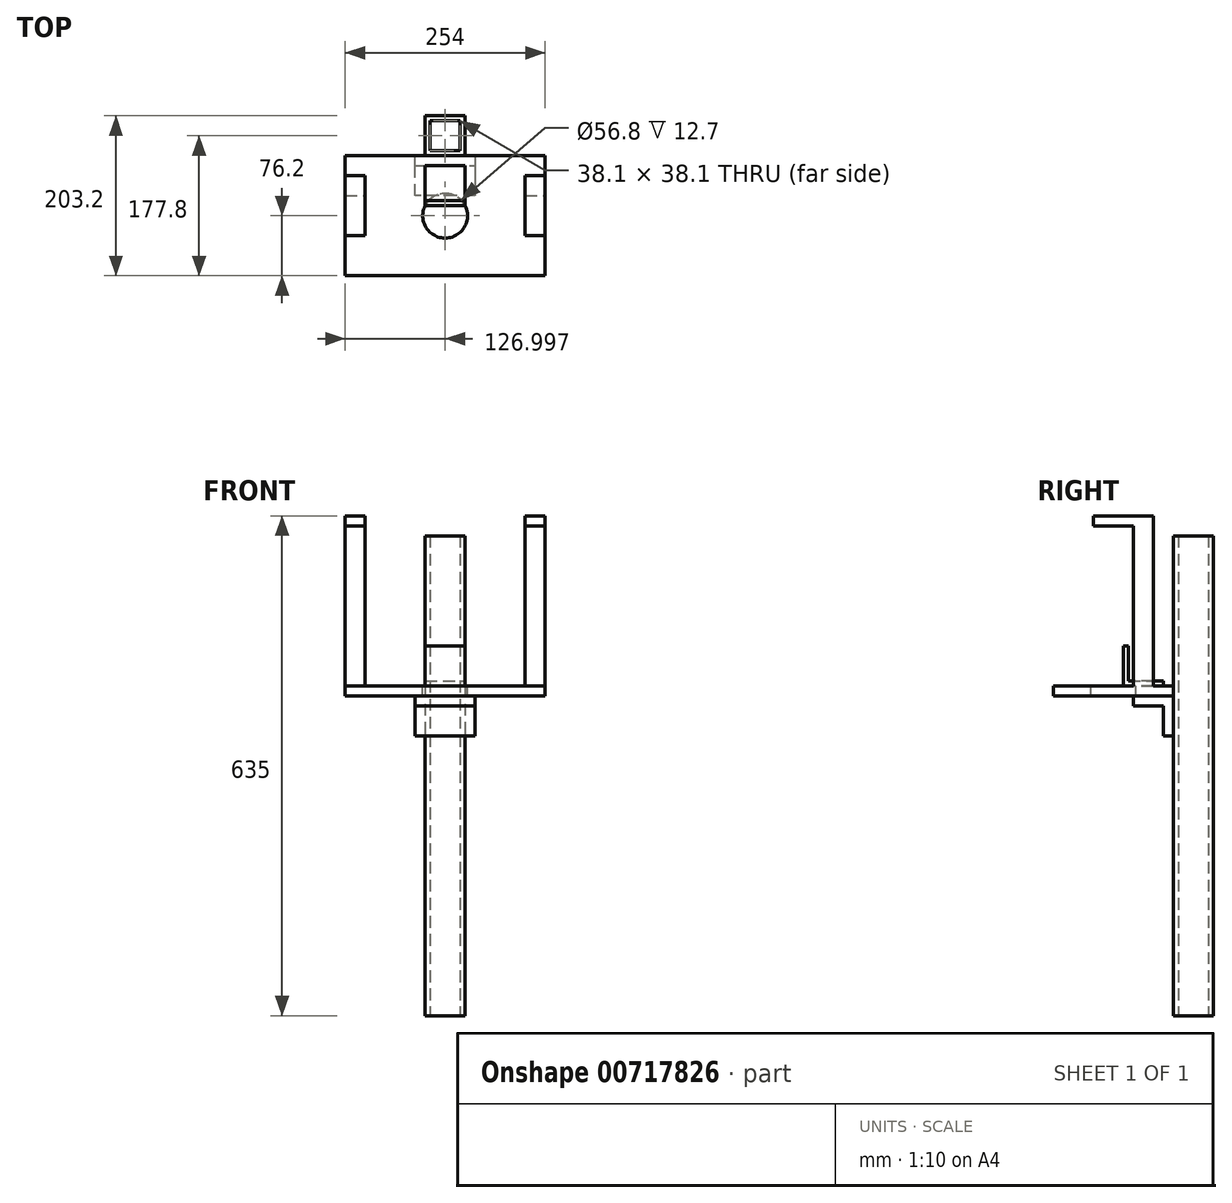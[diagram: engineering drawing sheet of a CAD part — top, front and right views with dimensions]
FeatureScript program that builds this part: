
annotation { "Feature Type Name" : "Feature", "Feature Type Description" : "" }
export const myFeature = defineFeature(function(context is Context, id is Id, definition is map)
    precondition{}
    {
        {
            var Q0;
            Q0=qCreatedBy(makeId("Top.planeOp"),FACE);
            var sketch = newSketch(context, id + "F0", { "sketchPlane" : qUnion([Q0])});
            skLineSegment(sketch, "E0.bottom", {"start": v(3.34, 0) * mm, "end": v(257.34, 0) * mm});
            skLineSegment(sketch, "E0.top", {"start": v(3.34, 152.4) * mm, "end": v(257.34, 152.4) * mm});
            skLineSegment(sketch, "E0.left", {"start": v(3.34, 0) * mm, "end": v(3.34, 152.4) * mm});
            skLineSegment(sketch, "E0.right", {"start": v(257.34, 0) * mm, "end": v(257.34, 152.4) * mm});
            skSolve(sketch);
        }
        {
            var Q0;
            Q0 = qSketchRegion(id + "F0", true);
            extrude(context, id + "F1", {"entities" : qUnion([Q0]), "depth" : 12.7 * mm, "offsetDistance" : 25.4 * mm});
        }
        {
            var Q0;
            Q0=makeQuery(id+"F1.opExtrude","CAP_FACE",FACE,{"disambiguationData":[OSD([sQuery(id+"F0.wireOp",EDGE,"E0.bottom"),sQuery(id+"F0.wireOp",EDGE,"E0.top"),sQuery(id+"F0.wireOp",EDGE,"E0.left"),sQuery(id+"F0.wireOp",EDGE,"E0.right")])],"isStart":false});
            var sketch = newSketch(context, id + "F2", { "sketchPlane" : qUnion([Q0])});
            skLineSegment(sketch, "E1", {"start": v(3.34, 88.9) * mm, "end": v(104.94, 88.9) * mm});
            skLineSegment(sketch, "E2", {"start": v(104.94, 88.9) * mm, "end": v(104.94, 139.7) * mm});
            skLineSegment(sketch, "E3", {"start": v(104.94, 139.7) * mm, "end": v(155.74, 139.7) * mm});
            skLineSegment(sketch, "E4", {"start": v(155.74, 139.7) * mm, "end": v(155.74, 88.9) * mm});
            skLineSegment(sketch, "E5", {"start": v(155.74, 88.9) * mm, "end": v(104.94, 88.9) * mm});
            skSolve(sketch);
        }
        {
            var Q0;
            Q0 = qSketchRegion(id + "F2", true);
            extrude(context, id + "F3", {"entities" : qUnion([Q0]), "operationType" : NewBodyOperationType.ADD, "depth" : 6.35 * mm, "offsetDistance" : 25.4 * mm});
        }
        {
            var Q0;
            Q0=makeQuery(id+"F3.opExtrude","CAP_FACE",FACE,{"disambiguationData":[OSD([sQuery(id+"F2.wireOp",EDGE,"E2"),sQuery(id+"F2.wireOp",EDGE,"E3"),sQuery(id+"F2.wireOp",EDGE,"E4"),sQuery(id+"F2.wireOp",EDGE,"E5")])],"isStart":false});
            var sketch = newSketch(context, id + "F4", { "sketchPlane" : qUnion([Q0])});
            skLineSegment(sketch, "E6", {"start": v(104.94, 88.9) * mm, "end": v(104.94, 95.25) * mm});
            skLineSegment(sketch, "E7", {"start": v(104.94, 95.25) * mm, "end": v(155.74, 95.25) * mm});
            skLineSegment(sketch, "E8", {"start": v(155.74, 95.25) * mm, "end": v(155.74, 88.9) * mm});
            skLineSegment(sketch, "E9", {"start": v(155.74, 88.9) * mm, "end": v(104.94, 88.9) * mm});
            skSolve(sketch);
        }
        {
            var Q0;
            Q0 = qSketchRegion(id + "F4", true);
            extrude(context, id + "F5", {"entities" : qUnion([Q0]), "operationType" : NewBodyOperationType.ADD, "depth" : 44.45 * mm, "offsetDistance" : 25.4 * mm});
        }
        {
            var Q0;
            Q0=makeQuery(id+"F1.opExtrude","CAP_FACE",FACE,{"disambiguationData":[OSD([sQuery(id+"F0.wireOp",EDGE,"E0.bottom"),sQuery(id+"F0.wireOp",EDGE,"E0.top"),sQuery(id+"F0.wireOp",EDGE,"E0.left"),sQuery(id+"F0.wireOp",EDGE,"E0.right")])],"isStart":false});
            var sketch = newSketch(context, id + "F6", { "sketchPlane" : qUnion([Q0])});
            skLineSegment(sketch, "E10", {"start": v(155.74, 88.9) * mm, "end": v(104.94, 88.9) * mm});
            skCircle(sketch, "E11", {"center": v(130.34, 76.2) * mm, "radius": 28.4 * mm});
            skSolve(sketch);
        }
        {
            var Q0;
            Q0 = qSketchRegion(id + "F6", true);
            extrude(context, id + "F7", {"entities" : qUnion([Q0]), "operationType" : NewBodyOperationType.REMOVE, "oppositeDirection" : true, "depth" : 25.4 * mm, "offsetDistance" : 25.4 * mm});
        }
        {
            var Q0;
            Q0=makeQuery(id+"F1.opExtrude","CAP_FACE",FACE,{"disambiguationData":[OSD([sQuery(id+"F0.wireOp",EDGE,"E0.bottom"),sQuery(id+"F0.wireOp",EDGE,"E0.top"),sQuery(id+"F0.wireOp",EDGE,"E0.left"),sQuery(id+"F0.wireOp",EDGE,"E0.right")])],"isStart":true});
            var sketch = newSketch(context, id + "F8", { "sketchPlane" : qUnion([Q0])});
            skLineSegment(sketch, "E12", {"start": v(130.34, -152.4) * mm, "end": v(168.44, -152.4) * mm});
            skLineSegment(sketch, "E13", {"start": v(168.44, -152.4) * mm, "end": v(168.44, -101.6) * mm});
            skLineSegment(sketch, "E14", {"start": v(168.44, -101.6) * mm, "end": v(92.24, -101.6) * mm});
            skLineSegment(sketch, "E15", {"start": v(92.24, -101.6) * mm, "end": v(92.24, -152.4) * mm});
            skLineSegment(sketch, "E16", {"start": v(92.24, -152.4) * mm, "end": v(130.34, -152.4) * mm});
            skSolve(sketch);
        }
        {
            var Q0;
            Q0 = qSketchRegion(id + "F8", true);
            extrude(context, id + "F9", {"entities" : qUnion([Q0]), "operationType" : NewBodyOperationType.ADD, "depth" : 12.7 * mm, "offsetDistance" : 25.4 * mm});
        }
        {
            var Q0;
            Q0=makeQuery(id+"F9.opExtrude","CAP_FACE",FACE,{"disambiguationData":[OSD([sQuery(id+"F8.wireOp",EDGE,"E12"),sQuery(id+"F8.wireOp",EDGE,"E13"),sQuery(id+"F8.wireOp",EDGE,"E14"),sQuery(id+"F8.wireOp",EDGE,"E15"),sQuery(id+"F8.wireOp",EDGE,"E16")])],"isStart":false});
            var sketch = newSketch(context, id + "F10", { "sketchPlane" : qUnion([Q0])});
            skLineSegment(sketch, "E17", {"start": v(92.24, -152.4) * mm, "end": v(92.24, -139.7) * mm});
            skLineSegment(sketch, "E18", {"start": v(92.24, -139.7) * mm, "end": v(168.44, -139.7) * mm});
            skLineSegment(sketch, "E19", {"start": v(168.44, -139.7) * mm, "end": v(168.44, -152.4) * mm});
            skLineSegment(sketch, "E20", {"start": v(168.44, -152.4) * mm, "end": v(92.24, -152.4) * mm});
            skSolve(sketch);
        }
        {
            var Q0;
            Q0 = qSketchRegion(id + "F10", true);
            extrude(context, id + "F11", {"entities" : qUnion([Q0]), "operationType" : NewBodyOperationType.ADD, "depth" : 38.1 * mm, "offsetDistance" : 25.4 * mm});
        }
        {
            var Q0;
            Q0=makeQuery(id+"F11.boolean.opBoolean","MERGE",FACE,{"derivedFrom":[makeQuery(id+"F9.boolean.opBoolean","MERGE",FACE,{"derivedFrom":[makeQuery(id+"F1.opExtrude","SWEPT_FACE",FACE,{"disambiguationData":[OSD([sQuery(id+"F0.wireOp",EDGE,"E0.top")])]}),makeQuery(id+"F9.opExtrude","SWEPT_FACE",FACE,{"disambiguationData":[OSD([sQuery(id+"F8.wireOp",EDGE,"E12"),sQuery(id+"F8.wireOp",EDGE,"E16")])]})]}),makeQuery(id+"F11.opExtrude","SWEPT_FACE",FACE,{"disambiguationData":[OSD([sQuery(id+"F10.wireOp",EDGE,"E20")])]})]});
            var sketch = newSketch(context, id + "F12", { "sketchPlane" : qUnion([Q0])});
            skLineSegment(sketch, "E21", {"start": v(-130.34, 203.2) * mm, "end": v(-155.74, 203.2) * mm});
            skLineSegment(sketch, "E22", {"start": v(-155.74, 203.2) * mm, "end": v(-155.74, -406.4) * mm});
            skLineSegment(sketch, "E23", {"start": v(-130.34, 203.2) * mm, "end": v(-104.94, 203.2) * mm});
            skLineSegment(sketch, "E24", {"start": v(-104.94, 203.2) * mm, "end": v(-104.94, -406.4) * mm});
            skLineSegment(sketch, "E25", {"start": v(-104.94, -406.4) * mm, "end": v(-155.74, -406.4) * mm});
            skSolve(sketch);
        }
        {
            var Q0;
            Q0 = qSketchRegion(id + "F12", true);
            extrude(context, id + "F13", {"entities" : qUnion([Q0]), "operationType" : NewBodyOperationType.ADD, "depth" : 50.8 * mm, "offsetDistance" : 25.4 * mm});
        }
        {
            var Q0;
            Q0=makeQuery(id+"F13.opExtrude","SWEPT_FACE",FACE,{"disambiguationData":[OSD([sQuery(id+"F12.wireOp",EDGE,"E25")])]});
            var sketch = newSketch(context, id + "F14", { "sketchPlane" : qUnion([Q0])});
            skLineSegment(sketch, "E26", {"start": v(104.94, -196.85) * mm, "end": v(111.29, -196.85) * mm});
            skLineSegment(sketch, "E27", {"start": v(111.29, -196.85) * mm, "end": v(111.29, -158.75) * mm});
            skLineSegment(sketch, "E28", {"start": v(111.29, -158.75) * mm, "end": v(149.39, -158.75) * mm});
            skLineSegment(sketch, "E29", {"start": v(149.39, -158.75) * mm, "end": v(149.39, -196.85) * mm});
            skLineSegment(sketch, "E30", {"start": v(149.39, -196.85) * mm, "end": v(111.29, -196.85) * mm});
            skSolve(sketch);
        }
        {
            var Q0;
            Q0 = qSketchRegion(id + "F14", true);
            extrude(context, id + "F15", {"entities" : qUnion([Q0]), "operationType" : NewBodyOperationType.REMOVE, "oppositeDirection" : true, "depth" : 647.7 * mm, "offsetDistance" : 25.4 * mm});
        }
        {
            var Q0;
            Q0=makeQuery(id+"F1.opExtrude","CAP_FACE",FACE,{"disambiguationData":[OSD([sQuery(id+"F0.wireOp",EDGE,"E0.bottom"),sQuery(id+"F0.wireOp",EDGE,"E0.top"),sQuery(id+"F0.wireOp",EDGE,"E0.left"),sQuery(id+"F0.wireOp",EDGE,"E0.right")])],"isStart":false});
            var sketch = newSketch(context, id + "F16", { "sketchPlane" : qUnion([Q0])});
            skLineSegment(sketch, "E31", {"start": v(3.34, 127) * mm, "end": v(28.74, 127) * mm});
            skLineSegment(sketch, "E32", {"start": v(28.74, 127) * mm, "end": v(28.74, 101.6) * mm});
            skLineSegment(sketch, "E33", {"start": v(3.34, 127) * mm, "end": v(3.34, 101.6) * mm});
            skLineSegment(sketch, "E34", {"start": v(3.34, 101.6) * mm, "end": v(28.74, 101.6) * mm});
            skLineSegment(sketch, "E35", {"start": v(257.34, 127) * mm, "end": v(231.94, 127) * mm});
            skLineSegment(sketch, "E36", {"start": v(231.94, 127) * mm, "end": v(231.94, 101.6) * mm});
            skLineSegment(sketch, "E37", {"start": v(231.94, 101.6) * mm, "end": v(257.34, 101.6) * mm});
            skLineSegment(sketch, "E38", {"start": v(257.34, 101.6) * mm, "end": v(257.34, 127) * mm});
            skSolve(sketch);
        }
        {
            var Q0;
            Q0 = qSketchRegion(id + "F16", true);
            extrude(context, id + "F17", {"entities" : qUnion([Q0]), "operationType" : NewBodyOperationType.ADD, "depth" : 203.2 * mm, "offsetDistance" : 25.4 * mm});
        }
        {
            var Q0;
            Q0=makeQuery(id+"F17.opExtrude","CAP_FACE",FACE,{"disambiguationData":[OSD([sQuery(id+"F16.wireOp",EDGE,"E35"),sQuery(id+"F16.wireOp",EDGE,"E36"),sQuery(id+"F16.wireOp",EDGE,"E37"),sQuery(id+"F16.wireOp",EDGE,"E38")])],"isStart":false});
            var sketch = newSketch(context, id + "F18", { "sketchPlane" : qUnion([Q0])});
            skLineSegment(sketch, "E39", {"start": v(231.94, 127) * mm, "end": v(257.34, 127) * mm});
            skLineSegment(sketch, "E40", {"start": v(257.34, 127) * mm, "end": v(257.34, 50.8) * mm});
            skLineSegment(sketch, "E41", {"start": v(257.34, 50.8) * mm, "end": v(231.94, 50.8) * mm});
            skLineSegment(sketch, "E42", {"start": v(231.94, 50.8) * mm, "end": v(231.94, 127) * mm});
            skSolve(sketch);
        }
        {
            var Q0;
            Q0 = qSketchRegion(id + "F18", true);
            extrude(context, id + "F19", {"entities" : qUnion([Q0]), "operationType" : NewBodyOperationType.ADD, "depth" : 12.7 * mm, "offsetDistance" : 25.4 * mm});
        }
        {
            var Q0;
            Q0=makeQuery(id+"F17.opExtrude","CAP_FACE",FACE,{"disambiguationData":[OSD([sQuery(id+"F16.wireOp",EDGE,"E31"),sQuery(id+"F16.wireOp",EDGE,"E32"),sQuery(id+"F16.wireOp",EDGE,"E33"),sQuery(id+"F16.wireOp",EDGE,"E34")])],"isStart":false});
            var sketch = newSketch(context, id + "F20", { "sketchPlane" : qUnion([Q0])});
            skLineSegment(sketch, "E43", {"start": v(3.34, 127) * mm, "end": v(3.34, 50.8) * mm});
            skLineSegment(sketch, "E44", {"start": v(3.34, 50.8) * mm, "end": v(28.74, 50.8) * mm});
            skLineSegment(sketch, "E45", {"start": v(28.74, 50.8) * mm, "end": v(28.74, 127) * mm});
            skLineSegment(sketch, "E46", {"start": v(28.74, 127) * mm, "end": v(3.34, 127) * mm});
            skSolve(sketch);
        }
        {
            var Q0;
            Q0 = qSketchRegion(id + "F20", true);
            extrude(context, id + "F21", {"entities" : qUnion([Q0]), "operationType" : NewBodyOperationType.ADD, "depth" : 12.7 * mm, "offsetDistance" : 25.4 * mm});
        }
    });
